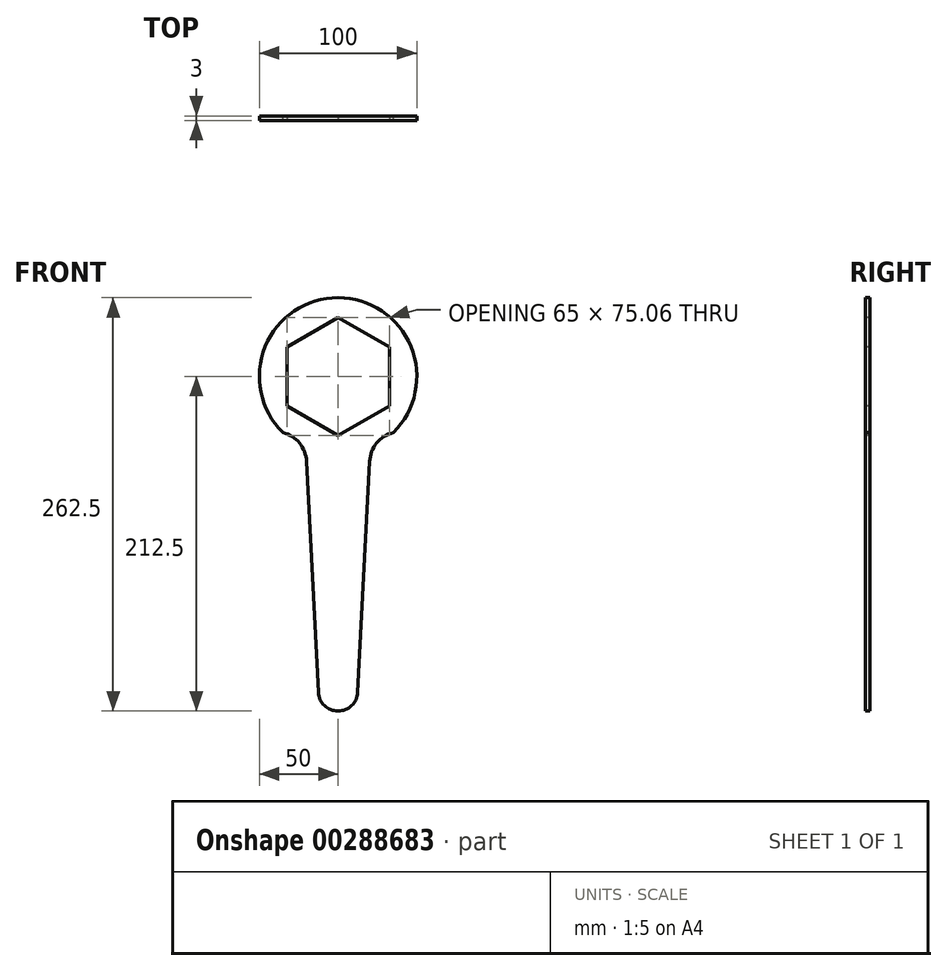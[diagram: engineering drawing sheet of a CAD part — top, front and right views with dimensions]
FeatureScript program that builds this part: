
annotation { "Feature Type Name" : "Feature", "Feature Type Description" : "" }
export const myFeature = defineFeature(function(context is Context, id is Id, definition is map)
    precondition{}
    {
        {
            var Q0;
            Q0=qCreatedBy(makeId("Front.planeOp"),FACE);
            var sketch = newSketch(context, id + "F0", { "sketchPlane" : qUnion([Q0])});
            skPoint(sketch, "E0", {"position": v(0, -200) * mm});
            skPoint(sketch, "E1", {"position": v(40, -55) * mm});
            skPoint(sketch, "E2", {"position": v(-40, -55) * mm});
            skArc(sketch, "E3", {"start": v(-20.03, -53.97) * mm, "mid": v(-24.54, -42.31) * mm, "end": v(-35.1, -35.6) * mm});
            skArc(sketch, "E4", {"start": v(35.1, -35.6) * mm, "mid": v(24.54, -42.31) * mm, "end": v(20.03, -53.97) * mm});
            skArc(sketch, "E5", {"start": v(-12.48, -200.64) * mm, "mid": v(0, -212.5) * mm, "end": v(12.48, -200.64) * mm});
            skLineSegment(sketch, "E6", {"start": v(-12.48, -200.64) * mm, "end": v(-20.03, -53.97) * mm});
            skLineSegment(sketch, "E7", {"start": v(12.48, -200.64) * mm, "end": v(20.03, -53.97) * mm});
            skArc(sketch, "E8.trimOffspring", {"start": v(35.1, -35.6) * mm, "mid": v(0, 50) * mm, "end": v(-35.1, -35.6) * mm});
            skSolve(sketch);
        }
        {
            var Q0;
            Q0=makeQuery(id+"F0.imprint","IMPRINT",FACE,{"disambiguationData":[TD([[makeQuery(id+"F0.imprint","IMPRINT",EDGE,{"derivedFrom":sQuery(id+"F0.wireOp",EDGE,"E3")}),-1.0]])]});
            extrude(context, id + "F1", {"entities" : qUnion([Q0]), "depth" : 3 * mm});
        }
        {
            var Q0;
            Q0=makeQuery(id+"F1.opExtrude","CAP_FACE",FACE,{"disambiguationData":[OSD([sQuery(id+"F0.wireOp",EDGE,"E3"),sQuery(id+"F0.wireOp",EDGE,"E4"),sQuery(id+"F0.wireOp",EDGE,"E5"),sQuery(id+"F0.wireOp",EDGE,"E6"),sQuery(id+"F0.wireOp",EDGE,"E7"),sQuery(id+"F0.wireOp",EDGE,"E8.trimOffspring")])],"isStart":false});
            var sketch = newSketch(context, id + "F2", { "sketchPlane" : qUnion([Q0])});
            skCircle(sketch, "E9.cCircle", {"center": v(0, 0) * mm, "radius": 32.5 * mm, "construction": true});
            skLineSegment(sketch, "E9.0", {"start": v(-32.5, -18.76) * mm, "end": v(-32.5, 18.76) * mm});
            skLineSegment(sketch, "E9.1", {"start": v(-32.5, 18.76) * mm, "end": v(0, 37.53) * mm});
            skLineSegment(sketch, "E9.2", {"start": v(0, 37.53) * mm, "end": v(32.5, 18.76) * mm});
            skLineSegment(sketch, "E9.3", {"start": v(32.5, 18.76) * mm, "end": v(32.5, -18.76) * mm});
            skLineSegment(sketch, "E9.4", {"start": v(32.5, -18.76) * mm, "end": v(0, -37.53) * mm});
            skLineSegment(sketch, "E9.5", {"start": v(0, -37.53) * mm, "end": v(-32.5, -18.76) * mm});
            skPoint(sketch, "E9.0.midPoint", {"position": v(-32.5, 0) * mm});
            skSolve(sketch);
        }
        {
            var Q0;
            Q0=makeQuery(id+"F2.imprint","IMPRINT",FACE,{"disambiguationData":[TD([[makeQuery(id+"F2.imprint","IMPRINT",EDGE,{"derivedFrom":sQuery(id+"F2.wireOp",EDGE,"E9.0")}),-1.0]])]});
            extrude(context, id + "F3", {"entities" : qUnion([Q0]), "operationType" : NewBodyOperationType.REMOVE, "oppositeDirection" : true, "depth" : 25 * mm});
        }
    });
